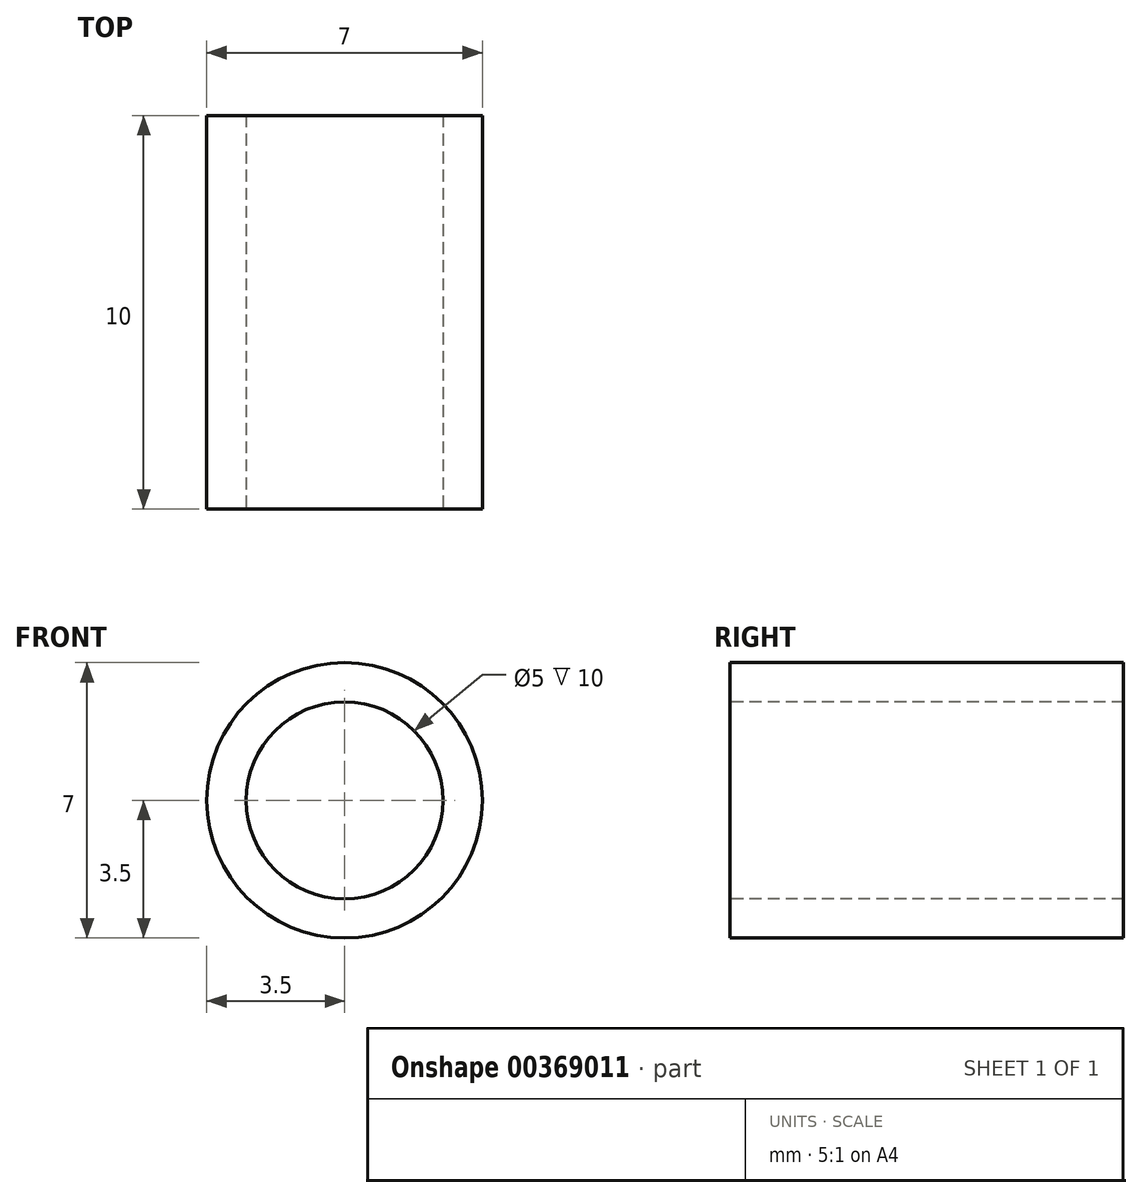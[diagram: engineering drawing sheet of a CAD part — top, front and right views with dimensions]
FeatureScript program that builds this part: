
annotation { "Feature Type Name" : "Feature", "Feature Type Description" : "" }
export const myFeature = defineFeature(function(context is Context, id is Id, definition is map)
    precondition{}
    {
        {
            var Q0;
            Q0=qCreatedBy(makeId("Front.planeOp"),FACE);
            var sketch = newSketch(context, id + "F0", { "sketchPlane" : qUnion([Q0])});
            skCircle(sketch, "E0", {"center": v(0, 0) * mm, "radius": 3.5 * mm});
            skSolve(sketch);
        }
        {
            var Q0;
            Q0=makeQuery(id+"F0.imprint","IMPRINT",FACE,{"disambiguationData":[TD([[makeQuery(id+"F0.imprint","IMPRINT",EDGE,{"derivedFrom":sQuery(id+"F0.wireOp",EDGE,"E0")}),1.0]])]});
            extrude(context, id + "F1", {"entities" : qUnion([Q0]), "endBound" : BoundingType.SYMMETRIC, "depth" : 10 * mm});
        }
        {
            var Q0;
            Q0=makeQuery(id+"F1.opExtrude","CAP_FACE",FACE,{"disambiguationData":[OSD([sQuery(id+"F0.wireOp",EDGE,"E0")])],"isStart":false});
            var sketch = newSketch(context, id + "F2", { "sketchPlane" : qUnion([Q0])});
            skCircle(sketch, "E1", {"center": v(0, 0) * mm, "radius": 2.5 * mm});
            skSolve(sketch);
        }
        {
            var Q0;
            Q0=makeQuery(id+"F2.imprint","IMPRINT",FACE,{"disambiguationData":[TD([[makeQuery(id+"F2.imprint","IMPRINT",EDGE,{"derivedFrom":sQuery(id+"F2.wireOp",EDGE,"E1")}),1.0]])]});
            extrude(context, id + "F3", {"entities" : qUnion([Q0]), "operationType" : NewBodyOperationType.REMOVE, "endBound" : BoundingType.THROUGH_ALL, "oppositeDirection" : true, "depth" : 25 * mm});
        }
    });
